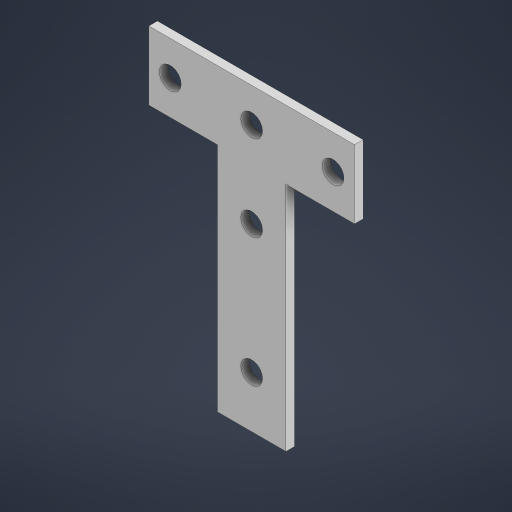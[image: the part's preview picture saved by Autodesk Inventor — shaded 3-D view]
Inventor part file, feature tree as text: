
AUTODESK INVENTOR PART (.ipt)
format: ipt  version: 2024 (Build 280153000, 153)  size: 189,952 bytes
history: native  units: mm
features: other x1, extrude x1, sketch x1
ambient origin geometry x8: Origin, YZ Plane, XZ Plane, XY Plane, X Axis, Y Axis, Z Axis, Center Point
bodies: Body1 (feature_tree)
feature tree (3):
  other  "Твердое тело1"
  extrude  "Выдавливание1"  Depth=16.0mm
  sketch  "Эскиз1"
